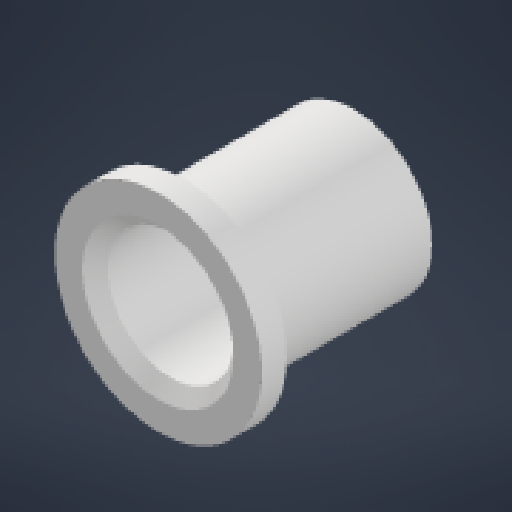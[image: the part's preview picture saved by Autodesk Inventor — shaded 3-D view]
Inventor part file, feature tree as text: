
AUTODESK INVENTOR PART (.ipt)
format: ipt  version: 2024.1 (Build 281209000, 209)  size: 144,384 bytes
history: native  units: in
note: dims shown in document units (in); Inventor stores cm internally (conversion verified against a paired STEP export)
features: other x3, extrude x2, sketch x1, chamfer x1, reference x1
ambient origin geometry x8: Origin, YZ Plane, XZ Plane, XY Plane, X Axis, Y Axis, Z Axis, Center Point
bodies: Solid1 (feature_tree)
feature tree (8):
  sketch  "Sketch1"  dims[d0=0.002in d1=0.05in d2=0.25in d3=0.05in d4=0.0in d5=0.3381in d6=0.0in d7=0.025in d8=0.125in d9=45.0deg]
  extrude  "Extrusion1"  Depth=0.05in
  extrude  "Extrusion2"  Depth=0.125in
  chamfer  "Chamfer1"  Distance=0.05in
  reference  "Reference1"
  other  "<userpath>\Documents\School\FallCAD\Trebuchet\Trebuchet.iam"
  other  "Trebuchet.iam"
  other  "BallBearing_8x22x7mm:10"
